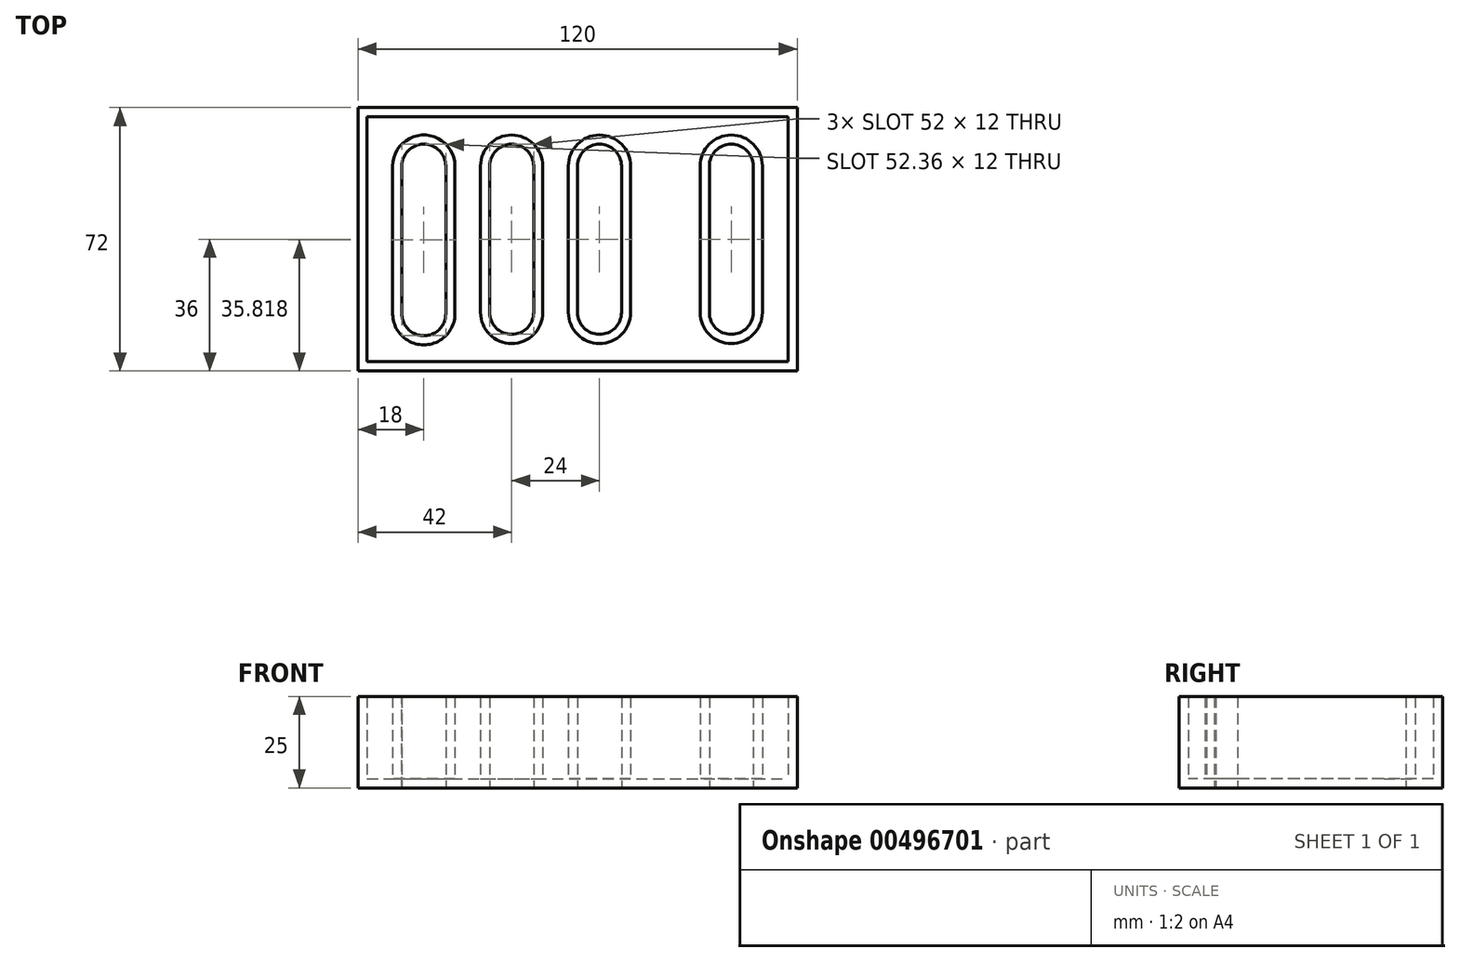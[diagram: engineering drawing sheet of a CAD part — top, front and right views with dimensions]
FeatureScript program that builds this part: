
annotation { "Feature Type Name" : "Feature", "Feature Type Description" : "" }
export const myFeature = defineFeature(function(context is Context, id is Id, definition is map)
    precondition{}
    {
        {
            var Q0;
            Q0=qCreatedBy(makeId("Top.planeOp"),FACE);
            var sketch = newSketch(context, id + "F0", { "sketchPlane" : qUnion([Q0])});
            skLineSegment(sketch, "E0.bottom", {"start": v(-60, 36) * mm, "end": v(60, 36) * mm});
            skLineSegment(sketch, "E0.top", {"start": v(-60, -36) * mm, "end": v(60, -36) * mm});
            skLineSegment(sketch, "E0.left", {"start": v(-60, 36) * mm, "end": v(-60, -36) * mm});
            skLineSegment(sketch, "E0.right", {"start": v(60, 36) * mm, "end": v(60, -36) * mm});
            skLineSegment(sketch, "E1", {"start": v(-48, 20) * mm, "end": v(-48, -20) * mm});
            skLineSegment(sketch, "E2", {"start": v(-36, 20) * mm, "end": v(-36, -20) * mm});
            skLineSegment(sketch, "E3", {"start": v(-24, 20) * mm, "end": v(-24, -20) * mm});
            skLineSegment(sketch, "E4", {"start": v(-12, 20) * mm, "end": v(-12, -20) * mm});
            skLineSegment(sketch, "E5", {"start": v(0, 20) * mm, "end": v(0, -20) * mm});
            skLineSegment(sketch, "E6", {"start": v(12, 20) * mm, "end": v(12, -20) * mm});
            skLineSegment(sketch, "E7", {"start": v(24, 20) * mm, "end": v(24, -20) * mm});
            skLineSegment(sketch, "E8", {"start": v(36, 20) * mm, "end": v(36, -20) * mm});
            skLineSegment(sketch, "E9", {"start": v(48, 20) * mm, "end": v(48, -20) * mm});
            skArc(sketch, "E10", {"start": v(-36, 20) * mm, "mid": v(-42, 26) * mm, "end": v(-48, 20) * mm});
            skArc(sketch, "E11", {"start": v(-48, -20) * mm, "mid": v(-42, -26.36) * mm, "end": v(-36, -20) * mm});
            skArc(sketch, "E12", {"start": v(-24, -20) * mm, "mid": v(-18, -26) * mm, "end": v(-12, -20) * mm});
            skArc(sketch, "E13", {"start": v(-12, 20) * mm, "mid": v(-18, 26) * mm, "end": v(-24, 20) * mm});
            skArc(sketch, "E14", {"start": v(12, 20) * mm, "mid": v(6, 26) * mm, "end": v(0, 20) * mm});
            skArc(sketch, "E15", {"start": v(0, -20) * mm, "mid": v(6, -26) * mm, "end": v(12, -20) * mm});
            skArc(sketch, "E16", {"start": v(48, 20) * mm, "mid": v(42, 26) * mm, "end": v(36, 20) * mm});
            skArc(sketch, "E17", {"start": v(36, -20) * mm, "mid": v(42, -26) * mm, "end": v(48, -20) * mm});
            skSolve(sketch);
        }
        {
            var Q0;
            Q0=makeQuery(id+"F0.imprint","IMPRINT",FACE,{"disambiguationData":[TD([[makeQuery(id+"F0.imprint","IMPRINT",EDGE,{"derivedFrom":sQuery(id+"F0.wireOp",EDGE,"E0.bottom")}),-1.0]])]});
            extrude(context, id + "F1", {"entities" : qUnion([Q0]), "depth" : 25 * mm});
        }
        {
            var Q0;
            Q0=makeQuery(id+"F1.opExtrude","CAP_FACE",FACE,{"disambiguationData":[OSD([sQuery(id+"F0.wireOp",EDGE,"E0.bottom"),sQuery(id+"F0.wireOp",EDGE,"E0.top"),sQuery(id+"F0.wireOp",EDGE,"E0.left"),sQuery(id+"F0.wireOp",EDGE,"E0.right"),sQuery(id+"F0.wireOp",EDGE,"E1"),sQuery(id+"F0.wireOp",EDGE,"E2"),sQuery(id+"F0.wireOp",EDGE,"E3"),sQuery(id+"F0.wireOp",EDGE,"E4"),sQuery(id+"F0.wireOp",EDGE,"E5"),sQuery(id+"F0.wireOp",EDGE,"E6"),sQuery(id+"F0.wireOp",EDGE,"E8"),sQuery(id+"F0.wireOp",EDGE,"E9"),sQuery(id+"F0.wireOp",EDGE,"E10"),sQuery(id+"F0.wireOp",EDGE,"E11"),sQuery(id+"F0.wireOp",EDGE,"E12"),sQuery(id+"F0.wireOp",EDGE,"E13"),sQuery(id+"F0.wireOp",EDGE,"E14"),sQuery(id+"F0.wireOp",EDGE,"E15"),sQuery(id+"F0.wireOp",EDGE,"E16"),sQuery(id+"F0.wireOp",EDGE,"E17")])],"isStart":false});
            shell(context, id + "F2", {"entities" : qUnion([Q0]), "thickness" : 2.5 * mm});
        }
    });
